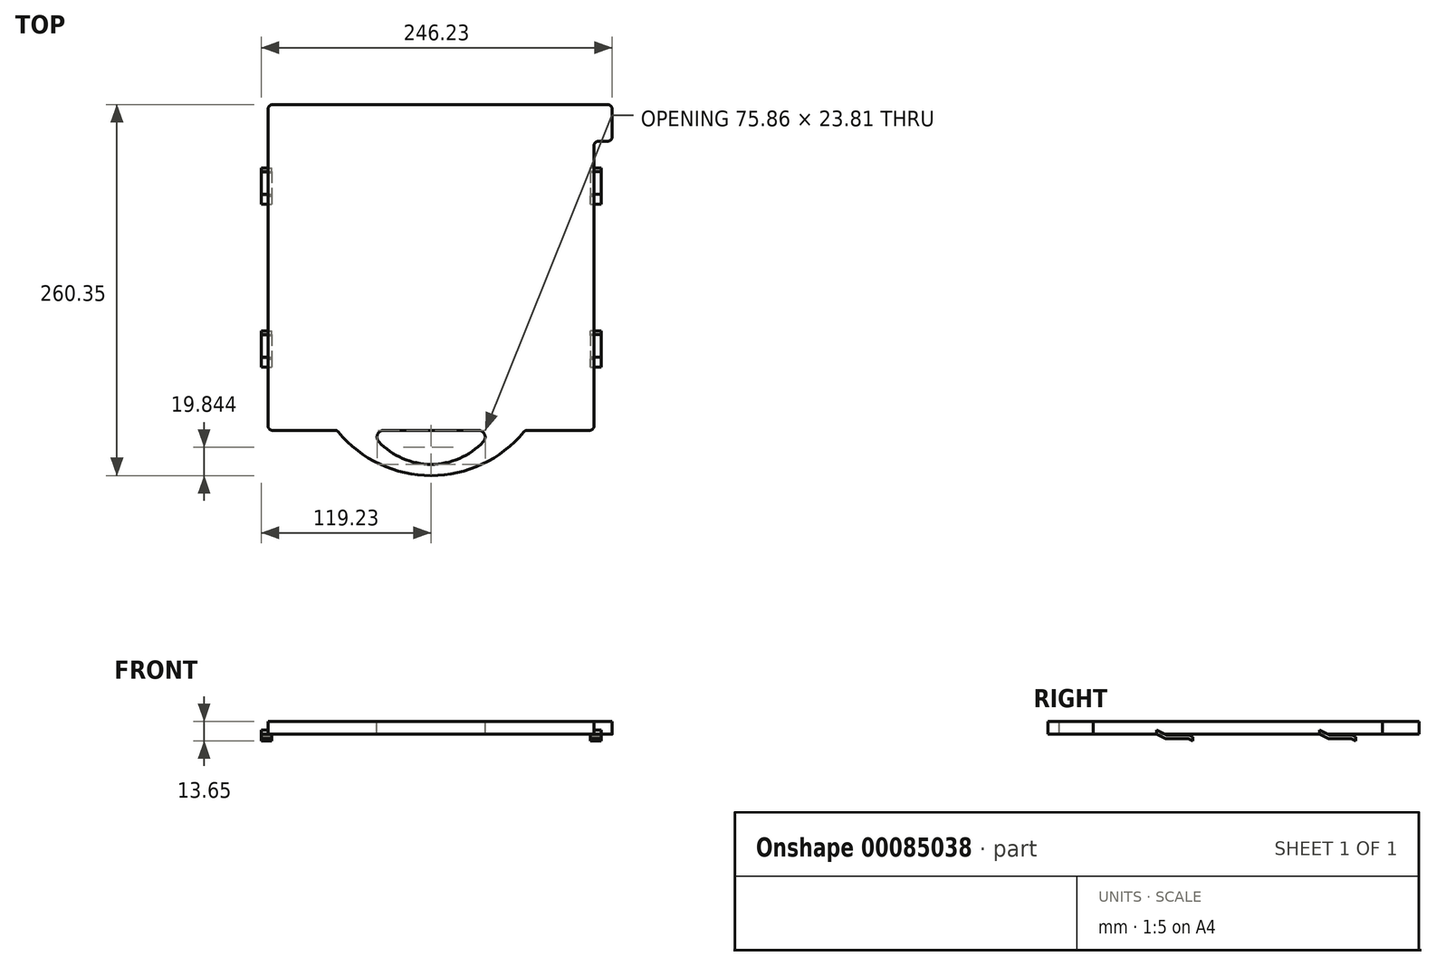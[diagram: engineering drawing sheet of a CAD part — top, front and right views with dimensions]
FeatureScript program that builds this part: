
annotation { "Feature Type Name" : "Feature", "Feature Type Description" : "" }
export const myFeature = defineFeature(function(context is Context, id is Id, definition is map)
    precondition{}
    {
        {
            var Q0;
            Q0=qCreatedBy(makeId("Top.planeOp"),FACE);
            var sketch = newSketch(context, id + "F0", { "sketchPlane" : qUnion([Q0])});
            skLineSegment(sketch, "E0.bottom", {"start": v(111.13, -114.3) * mm, "end": v(67.4, -114.3) * mm});
            skLineSegment(sketch, "E0.top", {"start": v(114.3, 114.3) * mm, "end": v(-111.13, 114.3) * mm});
            skLineSegment(sketch, "E0.left", {"start": v(114.3, -111.13) * mm, "end": v(114.3, 85.34) * mm});
            skLineSegment(sketch, "E0.right", {"start": v(-114.3, -111.13) * mm, "end": v(-114.3, 111.13) * mm});
            skPoint(sketch, "E0.middle", {"position": v(0, 0) * mm});
            skLineSegment(sketch, "E1.bottom", {"start": v(114.3, 114.3) * mm, "end": v(123.83, 114.3) * mm});
            skLineSegment(sketch, "E1.top", {"start": v(117.47, 88.52) * mm, "end": v(123.83, 88.52) * mm});
            skLineSegment(sketch, "E1.right", {"start": v(127, 111.13) * mm, "end": v(127, 91.7) * mm});
            skArc(sketch, "E2", {"start": v(-64.95, -115.45) * mm, "mid": v(0, -146.05) * mm, "end": v(64.95, -115.45) * mm});
            skLineSegment(sketch, "E3.trimOffspring", {"start": v(-67.4, -114.3) * mm, "end": v(-111.13, -114.3) * mm});
            skPoint(sketch, "E4.visualSharp", {"position": v(127, 114.3) * mm});
            skArc(sketch, "E4.filletArc", {"start": v(127, 111.13) * mm, "mid": v(126.07, 113.37) * mm, "end": v(123.83, 114.3) * mm});
            skPoint(sketch, "E5.visualSharp", {"position": v(127, 88.52) * mm});
            skArc(sketch, "E5.filletArc", {"start": v(123.83, 88.52) * mm, "mid": v(126.07, 89.45) * mm, "end": v(127, 91.7) * mm});
            skPoint(sketch, "E6.visualSharp", {"position": v(-114.3, 114.3) * mm});
            skArc(sketch, "E6.filletArc", {"start": v(-111.13, 114.3) * mm, "mid": v(-113.37, 113.37) * mm, "end": v(-114.3, 111.13) * mm});
            skPoint(sketch, "E7.visualSharp", {"position": v(-114.3, -114.3) * mm});
            skArc(sketch, "E7.filletArc", {"start": v(-114.3, -111.13) * mm, "mid": v(-113.37, -113.37) * mm, "end": v(-111.13, -114.3) * mm});
            skPoint(sketch, "E8.visualSharp", {"position": v(-65.88, -114.3) * mm});
            skArc(sketch, "E8.filletArc", {"start": v(-64.95, -115.45) * mm, "mid": v(-66.04, -114.6) * mm, "end": v(-67.4, -114.3) * mm});
            skPoint(sketch, "E9.visualSharp", {"position": v(65.88, -114.3) * mm});
            skArc(sketch, "E9.filletArc", {"start": v(67.4, -114.3) * mm, "mid": v(66.04, -114.6) * mm, "end": v(64.95, -115.45) * mm});
            skPoint(sketch, "E10.visualSharp", {"position": v(114.3, -114.3) * mm});
            skArc(sketch, "E10.filletArc", {"start": v(111.13, -114.3) * mm, "mid": v(113.37, -113.37) * mm, "end": v(114.3, -111.13) * mm});
            skPoint(sketch, "E11.visualSharp", {"position": v(114.3, 88.52) * mm});
            skArc(sketch, "E11.filletArc", {"start": v(117.47, 88.52) * mm, "mid": v(115.23, 87.59) * mm, "end": v(114.3, 85.34) * mm});
            skSolve(sketch);
        }
        {
            var Q0;
            Q0=makeQuery(id+"F0.imprint","IMPRINT",FACE,{"disambiguationData":[TD([[makeQuery(id+"F0.imprint","IMPRINT",EDGE,{"derivedFrom":sQuery(id+"F0.wireOp",EDGE,"E0.bottom")}),-1.0]])]});
            extrude(context, id + "F1", {"entities" : qUnion([Q0]), "depth" : 8.9 * mm});
        }
        {
            var Q0;
            Q0=makeQuery(id+"F1.opExtrude","SWEPT_FACE",FACE,{"disambiguationData":[OSD([sQuery(id+"F0.wireOp",EDGE,"E0.left")])]});
            var sketch = newSketch(context, id + "F2", { "sketchPlane" : qUnion([Q0])});
            skPoint(sketch, "E12.0", {"position": v(114.3, 0) * mm});
            skLineSegment(sketch, "E13", {"start": v(114.3, 0) * mm, "end": v(111.12, 0) * mm, "construction": true});
            skLineSegment(sketch, "E14", {"start": v(66.68, -3.18) * mm, "end": v(50.8, -3.18) * mm});
            skLineSegment(sketch, "E15", {"start": v(50.8, -3.17) * mm, "end": v(44.45, 0) * mm});
            skLineSegment(sketch, "E16", {"start": v(66.68, -3.17) * mm, "end": v(69.85, -4.76) * mm});
            skLineSegment(sketch, "E17.0", {"start": v(-111.13, 0) * mm, "end": v(44.45, 0) * mm});
            skPoint(sketch, "E18.orphan", {"position": v(111.12, 0) * mm});
            skLineSegment(sketch, "E19.0", {"start": v(51.4, -0.64) * mm, "end": v(44.45, 2.84) * mm});
            skLineSegment(sketch, "E19.1", {"start": v(67.27, -0.63) * mm, "end": v(51.4, -0.64) * mm});
            skLineSegment(sketch, "E19.2", {"start": v(67.27, -0.63) * mm, "end": v(69.85, -1.92) * mm});
            skLineSegment(sketch, "E20", {"start": v(44.45, 0) * mm, "end": v(44.45, 2.84) * mm});
            skLineSegment(sketch, "E21", {"start": v(69.85, -4.76) * mm, "end": v(69.85, -1.92) * mm});
            skSolve(sketch);
        }
        {
            var Q0;
            Q0=makeQuery(id+"F2.imprint","IMPRINT",FACE,{"disambiguationData":[TD([[makeQuery(id+"F2.imprint","IMPRINT",EDGE,{"derivedFrom":sQuery(id+"F2.wireOp",EDGE,"E14")}),-1.0]])]});
            var Q1;
            {var subQ0=sQuery(id+"F2.wireOp",EDGE,"E20");Q1=makeQuery(id+"F2.imprint","IMPRINT",FACE,{"disambiguationData":[TD([[makeQuery(id+"F2.imprint","IMPRINT",EDGE,{"derivedFrom":subQ0}),-1.0]])]});}
            extrude(context, id + "F3", {"entities" : qUnion([Q0, Q1]), "depth" : 4.93 * mm, "hasSecondDirection" : true, "secondDirectionOppositeDirection" : true, "secondDirectionDepth" : 2.54 * mm});
        }
        {
            var Q0;
            Q0=makeQuery(id+"F3.opExtrude","SWEPT_BODY",BODY,{"disambiguationData":[OSD([sQuery(id+"F0.wireOp",EDGE,"E0.left"),sQuery(id+"F2.wireOp",EDGE,"E14"),sQuery(id+"F2.wireOp",EDGE,"E15"),sQuery(id+"F2.wireOp",EDGE,"E16"),sQuery(id+"F2.wireOp",EDGE,"E19.0"),sQuery(id+"F2.wireOp",EDGE,"E19.1"),sQuery(id+"F2.wireOp",EDGE,"E19.2"),sQuery(id+"F2.wireOp",EDGE,"E21")])]});
            transform(context, id + "F4", {"entities" : qUnion([Q0]), "transformType" : TransformType.TRANSLATION_3D, "dx" : 0 * mm, "dy" : -114.3 * mm, "dz" : 0 * mm, "makeCopy" : true});
        }
        {
            var Q0;
            Q0=makeQuery(id+"F3.opExtrude","SWEPT_BODY",BODY,{"disambiguationData":[OSD([sQuery(id+"F0.wireOp",EDGE,"E0.left"),sQuery(id+"F2.wireOp",EDGE,"E14"),sQuery(id+"F2.wireOp",EDGE,"E15"),sQuery(id+"F2.wireOp",EDGE,"E16"),sQuery(id+"F2.wireOp",EDGE,"E19.0"),sQuery(id+"F2.wireOp",EDGE,"E19.1"),sQuery(id+"F2.wireOp",EDGE,"E19.2"),sQuery(id+"F2.wireOp",EDGE,"E21")])]});
            var Q1;
            Q1=makeQuery(id+"F4.opPattern","COPY",BODY,{"derivedFrom":makeQuery(id+"F3.opExtrude","SWEPT_BODY",BODY,{"disambiguationData":[OSD([sQuery(id+"F0.wireOp",EDGE,"E0.left"),sQuery(id+"F2.wireOp",EDGE,"E14"),sQuery(id+"F2.wireOp",EDGE,"E15"),sQuery(id+"F2.wireOp",EDGE,"E16"),sQuery(id+"F2.wireOp",EDGE,"E19.0"),sQuery(id+"F2.wireOp",EDGE,"E19.1"),sQuery(id+"F2.wireOp",EDGE,"E19.2"),sQuery(id+"F2.wireOp",EDGE,"E21")])]}),"instanceName":"1"});
            var Q2;
            Q2=qCreatedBy(makeId("Right.planeOp"),FACE);
            mirror(context, id + "F5", {"operationType" : NewBodyOperationType.ADD, "entities" : qUnion([Q0, Q1]), "mirrorPlane" : qUnion([Q2])});
        }
        {
            var Q0;
            Q0=makeQuery(id+"F1.opExtrude","CAP_FACE",FACE,{"disambiguationData":[OSD([sQuery(id+"F0.wireOp",EDGE,"E0.bottom"),sQuery(id+"F0.wireOp",EDGE,"E0.top"),sQuery(id+"F0.wireOp",EDGE,"E0.left"),sQuery(id+"F0.wireOp",EDGE,"E0.right"),sQuery(id+"F0.wireOp",EDGE,"E1.bottom"),sQuery(id+"F0.wireOp",EDGE,"E1.top"),sQuery(id+"F0.wireOp",EDGE,"E1.right"),sQuery(id+"F0.wireOp",EDGE,"E2"),sQuery(id+"F0.wireOp",EDGE,"E3.trimOffspring"),sQuery(id+"F0.wireOp",EDGE,"E4.filletArc"),sQuery(id+"F0.wireOp",EDGE,"E5.filletArc"),sQuery(id+"F0.wireOp",EDGE,"E6.filletArc"),sQuery(id+"F0.wireOp",EDGE,"E7.filletArc"),sQuery(id+"F0.wireOp",EDGE,"E8.filletArc"),sQuery(id+"F0.wireOp",EDGE,"E9.filletArc"),sQuery(id+"F0.wireOp",EDGE,"E10.filletArc"),sQuery(id+"F0.wireOp",EDGE,"E11.filletArc")])],"isStart":false});
            var sketch = newSketch(context, id + "F6", { "sketchPlane" : qUnion([Q0])});
            skLineSegment(sketch, "E22", {"start": v(-33.2, -114.3) * mm, "end": v(33.2, -114.3) * mm});
            skLineSegment(sketch, "E23", {"start": v(0, -114.3) * mm, "end": v(0, -138.11) * mm, "construction": true});
            skPoint(sketch, "E23.endSnap0", {"position": v(0, -114.3) * mm});
            skArc(sketch, "E24", {"start": v(-36.66, -122.34) * mm, "mid": v(0, -138.11) * mm, "end": v(36.66, -122.34) * mm});
            skPoint(sketch, "E25.visualSharp", {"position": v(-42.86, -114.3) * mm});
            skArc(sketch, "E25.filletArc", {"start": v(-33.2, -114.3) * mm, "mid": v(-37.58, -117.18) * mm, "end": v(-36.66, -122.34) * mm});
            skPoint(sketch, "E26.visualSharp", {"position": v(42.86, -114.3) * mm});
            skArc(sketch, "E26.filletArc", {"start": v(36.66, -122.34) * mm, "mid": v(37.58, -117.18) * mm, "end": v(33.2, -114.3) * mm});
            skSolve(sketch);
        }
        {
            var Q0;
            Q0=makeQuery(id+"F6.imprint","IMPRINT",FACE,{"disambiguationData":[TD([[makeQuery(id+"F6.imprint","IMPRINT",EDGE,{"derivedFrom":sQuery(id+"F6.wireOp",EDGE,"E22")}),-1.0]])]});
            extrude(context, id + "F7", {"entities" : qUnion([Q0]), "operationType" : NewBodyOperationType.REMOVE, "endBound" : BoundingType.THROUGH_ALL, "oppositeDirection" : true, "depth" : 25.4 * mm});
        }
    });
